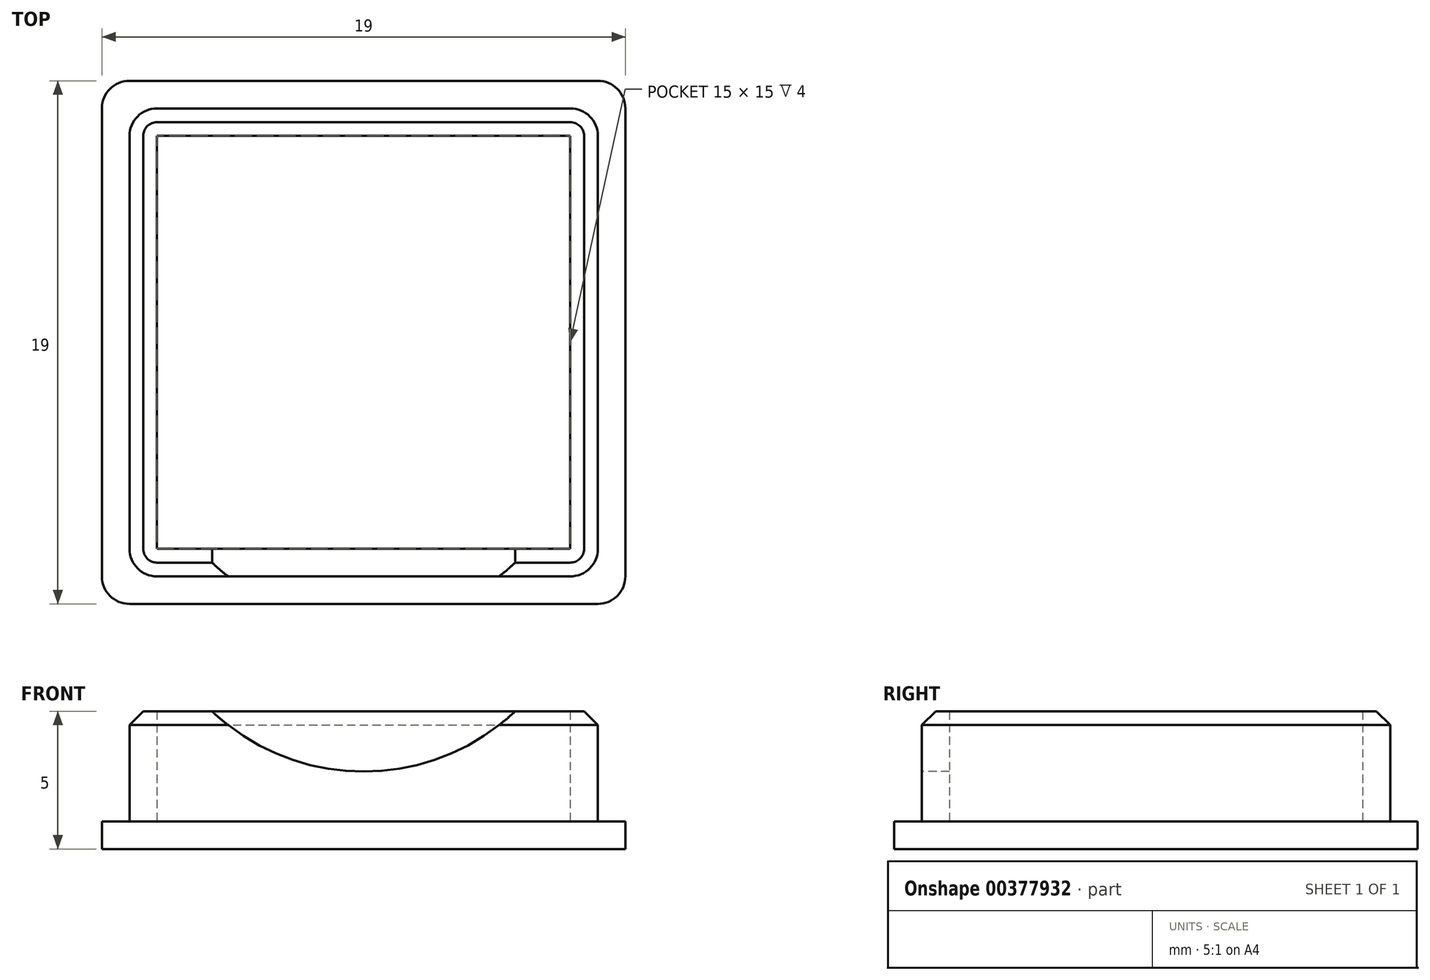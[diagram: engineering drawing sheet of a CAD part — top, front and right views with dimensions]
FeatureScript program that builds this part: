
annotation { "Feature Type Name" : "Feature", "Feature Type Description" : "" }
export const myFeature = defineFeature(function(context is Context, id is Id, definition is map)
    precondition{}
    {
        {
            var Q0;
            Q0=qCreatedBy(makeId("Top.planeOp"),FACE);
            var sketch = newSketch(context, id + "F0", { "sketchPlane" : qUnion([Q0])});
            skLineSegment(sketch, "E0.bottom", {"start": v(9.5, -9.5) * mm, "end": v(-9.5, -9.5) * mm});
            skLineSegment(sketch, "E0.top", {"start": v(9.5, 9.5) * mm, "end": v(-9.5, 9.5) * mm});
            skLineSegment(sketch, "E0.left", {"start": v(9.5, -9.5) * mm, "end": v(9.5, 9.5) * mm});
            skLineSegment(sketch, "E0.right", {"start": v(-9.5, -9.5) * mm, "end": v(-9.5, 9.5) * mm});
            skPoint(sketch, "E0.middle", {"position": v(0, 0) * mm});
            skSolve(sketch);
        }
        {
            var Q0;
            Q0 = qSketchRegion(id + "F0", true);
            extrude(context, id + "F1", {"entities" : qUnion([Q0]), "depth" : 1 * mm});
        }
        {
            var Q0;
            Q0=makeQuery(id+"F1.opExtrude","CAP_FACE",FACE,{"disambiguationData":[OSD([sQuery(id+"F0.wireOp",EDGE,"E0.bottom"),sQuery(id+"F0.wireOp",EDGE,"E0.top"),sQuery(id+"F0.wireOp",EDGE,"E0.left"),sQuery(id+"F0.wireOp",EDGE,"E0.right")])],"isStart":false});
            var sketch = newSketch(context, id + "F2", { "sketchPlane" : qUnion([Q0])});
            skLineSegment(sketch, "E1.bottom", {"start": v(8.5, 8.5) * mm, "end": v(-8.5, 8.5) * mm});
            skLineSegment(sketch, "E1.top", {"start": v(8.5, -8.5) * mm, "end": v(-8.5, -8.5) * mm});
            skLineSegment(sketch, "E1.left", {"start": v(8.5, 8.5) * mm, "end": v(8.5, -8.5) * mm});
            skLineSegment(sketch, "E1.right", {"start": v(-8.5, 8.5) * mm, "end": v(-8.5, -8.5) * mm});
            skPoint(sketch, "E1.middle", {"position": v(0, 0) * mm});
            skSolve(sketch);
        }
        {
            var Q0;
            Q0 = qSketchRegion(id + "F2", true);
            extrude(context, id + "F3", {"entities" : qUnion([Q0]), "operationType" : NewBodyOperationType.ADD, "depth" : 4 * mm});
        }
        {
            var Q0;
            Q0=makeQuery(id+"F3.opExtrude","CAP_FACE",FACE,{"disambiguationData":[OSD([sQuery(id+"F2.wireOp",EDGE,"E1.bottom"),sQuery(id+"F2.wireOp",EDGE,"E1.top"),sQuery(id+"F2.wireOp",EDGE,"E1.left"),sQuery(id+"F2.wireOp",EDGE,"E1.right")])],"isStart":false});
            shell(context, id + "F4", {"entities" : qUnion([Q0]), "thickness" : 1 * mm});
        }
        {
            var Q0;
            Q0=makeQuery(id+"F3.opExtrude","SWEPT_FACE",FACE,{"disambiguationData":[OSD([sQuery(id+"F2.wireOp",EDGE,"E1.top")])]});
            var sketch = newSketch(context, id + "F5", { "sketchPlane" : qUnion([Q0])});
            skLineSegment(sketch, "E2", {"start": v(-5.5, 5) * mm, "end": v(-5.5, 1) * mm, "construction": true});
            skLineSegment(sketch, "E3", {"start": v(5.5, 5) * mm, "end": v(5.5, 1) * mm, "construction": true});
            skArc(sketch, "E4", {"start": v(-5.5, 5) * mm, "mid": v(0, 2.8) * mm, "end": v(5.5, 5) * mm});
            skLineSegment(sketch, "E5", {"start": v(-5.5, 5) * mm, "end": v(5.5, 5) * mm});
            skSolve(sketch);
        }
        {
            var Q0;
            Q0 = qSketchRegion(id + "F5", true);
            extrude(context, id + "F6", {"entities" : qUnion([Q0]), "operationType" : NewBodyOperationType.REMOVE, "oppositeDirection" : true, "depth" : 2 * mm});
        }
        {
            var Q0;
            Q0=qCreatedBy(makeId("Front.planeOp"),FACE);
            var sketch = newSketch(context, id + "F7", { "sketchPlane" : qUnion([Q0])});
            skLineSegment(sketch, "E6", {"start": v(0, 0) * mm, "end": v(0, 19.53) * mm, "construction": true});
            skSolve(sketch);
        }
        {
            var Q0;
            Q0=makeQuery(id+"F3.opExtrude","SWEPT_EDGE",EDGE,{"disambiguationData":[OSD([sQuery(id+"F2.wireOp",EDGE,"E1.top"),sQuery(id+"F2.wireOp",EDGE,"E1.right")])]});
            var Q1;
            Q1=makeQuery(id+"F1.opExtrude","SWEPT_EDGE",EDGE,{"disambiguationData":[OSD([sQuery(id+"F0.wireOp",EDGE,"E0.bottom"),sQuery(id+"F0.wireOp",EDGE,"E0.right")])]});
            var Q2;
            Q2=makeQuery(id+"F3.opExtrude","SWEPT_EDGE",EDGE,{"disambiguationData":[OSD([sQuery(id+"F2.wireOp",EDGE,"E1.top"),sQuery(id+"F2.wireOp",EDGE,"E1.left")])]});
            var Q3;
            Q3=makeQuery(id+"F1.opExtrude","SWEPT_EDGE",EDGE,{"disambiguationData":[OSD([sQuery(id+"F0.wireOp",EDGE,"E0.bottom"),sQuery(id+"F0.wireOp",EDGE,"E0.left")])]});
            var Q4;
            Q4=makeQuery(id+"F3.opExtrude","SWEPT_EDGE",EDGE,{"disambiguationData":[OSD([sQuery(id+"F2.wireOp",EDGE,"E1.bottom"),sQuery(id+"F2.wireOp",EDGE,"E1.left")])]});
            var Q5;
            Q5=makeQuery(id+"F1.opExtrude","SWEPT_EDGE",EDGE,{"disambiguationData":[OSD([sQuery(id+"F0.wireOp",EDGE,"E0.top"),sQuery(id+"F0.wireOp",EDGE,"E0.left")])]});
            var Q6;
            Q6=makeQuery(id+"F3.opExtrude","SWEPT_EDGE",EDGE,{"disambiguationData":[OSD([sQuery(id+"F2.wireOp",EDGE,"E1.bottom"),sQuery(id+"F2.wireOp",EDGE,"E1.right")])]});
            var Q7;
            Q7=makeQuery(id+"F1.opExtrude","SWEPT_EDGE",EDGE,{"disambiguationData":[OSD([sQuery(id+"F0.wireOp",EDGE,"E0.top"),sQuery(id+"F0.wireOp",EDGE,"E0.right")])]});
            fillet(context, id + "F8", {"entities" : qUnion([Q0, Q1, Q2, Q3, Q4, Q5, Q6, Q7]), "radius" : 1 * mm, "tangentPropagation" : true, "allowEdgeOverflow" : false});
        }
        {
            var Q0;
            {var subQ0=sQuery(id+"F2.wireOp",EDGE,"E1.bottom");var subQ1=sQuery(id+"F2.wireOp",EDGE,"E1.right");Q0=makeQuery(id+"FqKu0fXsJ2oJxU0_1.2.F6.boolean.opBoolean","SPLIT",EDGE,{"disambiguationData":[TD([makeQuery(id+"F3.opExtrude","SWEPT_FACE",FACE,{"disambiguationData":[OSD([subQ1])]})])],"derivedFrom":makeQuery(id+"F3.opExtrude","CAP_EDGE",EDGE,{"disambiguationData":[OSD([subQ0])],"isStart":false})});}
            var Q1;
            {var subQ0=sQuery(id+"F2.wireOp",EDGE,"E1.right");var subQ1=sQuery(id+"F2.wireOp",EDGE,"E1.top");Q1=makeQuery(id+"FqKu0fXsJ2oJxU0_1.3.F6.boolean.opBoolean","SPLIT",EDGE,{"disambiguationData":[TD([makeQuery(id+"F3.opExtrude","SWEPT_FACE",FACE,{"disambiguationData":[OSD([subQ1])]})])],"derivedFrom":makeQuery(id+"F3.opExtrude","CAP_EDGE",EDGE,{"disambiguationData":[OSD([subQ0])],"isStart":false})});}
            var Q2;
            {var subQ0=sQuery(id+"F2.wireOp",EDGE,"E1.left");var subQ1=sQuery(id+"F2.wireOp",EDGE,"E1.top");Q2=makeQuery(id+"F6.boolean.opBoolean","SPLIT",EDGE,{"disambiguationData":[TD([makeQuery(id+"F3.opExtrude","SWEPT_FACE",FACE,{"disambiguationData":[OSD([subQ0])]})])],"derivedFrom":makeQuery(id+"F3.opExtrude","CAP_EDGE",EDGE,{"disambiguationData":[OSD([subQ1])],"isStart":false})});}
            var Q3;
            {var subQ0=sQuery(id+"F2.wireOp",EDGE,"E1.bottom");var subQ1=sQuery(id+"F2.wireOp",EDGE,"E1.left");Q3=makeQuery(id+"FqKu0fXsJ2oJxU0_1.1.F6.boolean.opBoolean","SPLIT",EDGE,{"disambiguationData":[TD([makeQuery(id+"F3.opExtrude","SWEPT_FACE",FACE,{"disambiguationData":[OSD([subQ0])]})])],"derivedFrom":makeQuery(id+"F3.opExtrude","CAP_EDGE",EDGE,{"disambiguationData":[OSD([subQ1])],"isStart":false})});}
            chamfer(context, id + "F9", {"entities" : qUnion([Q0, Q1, Q2, Q3]), "width" : 0.5 * mm, "tangentPropagation" : true});
        }
    });
